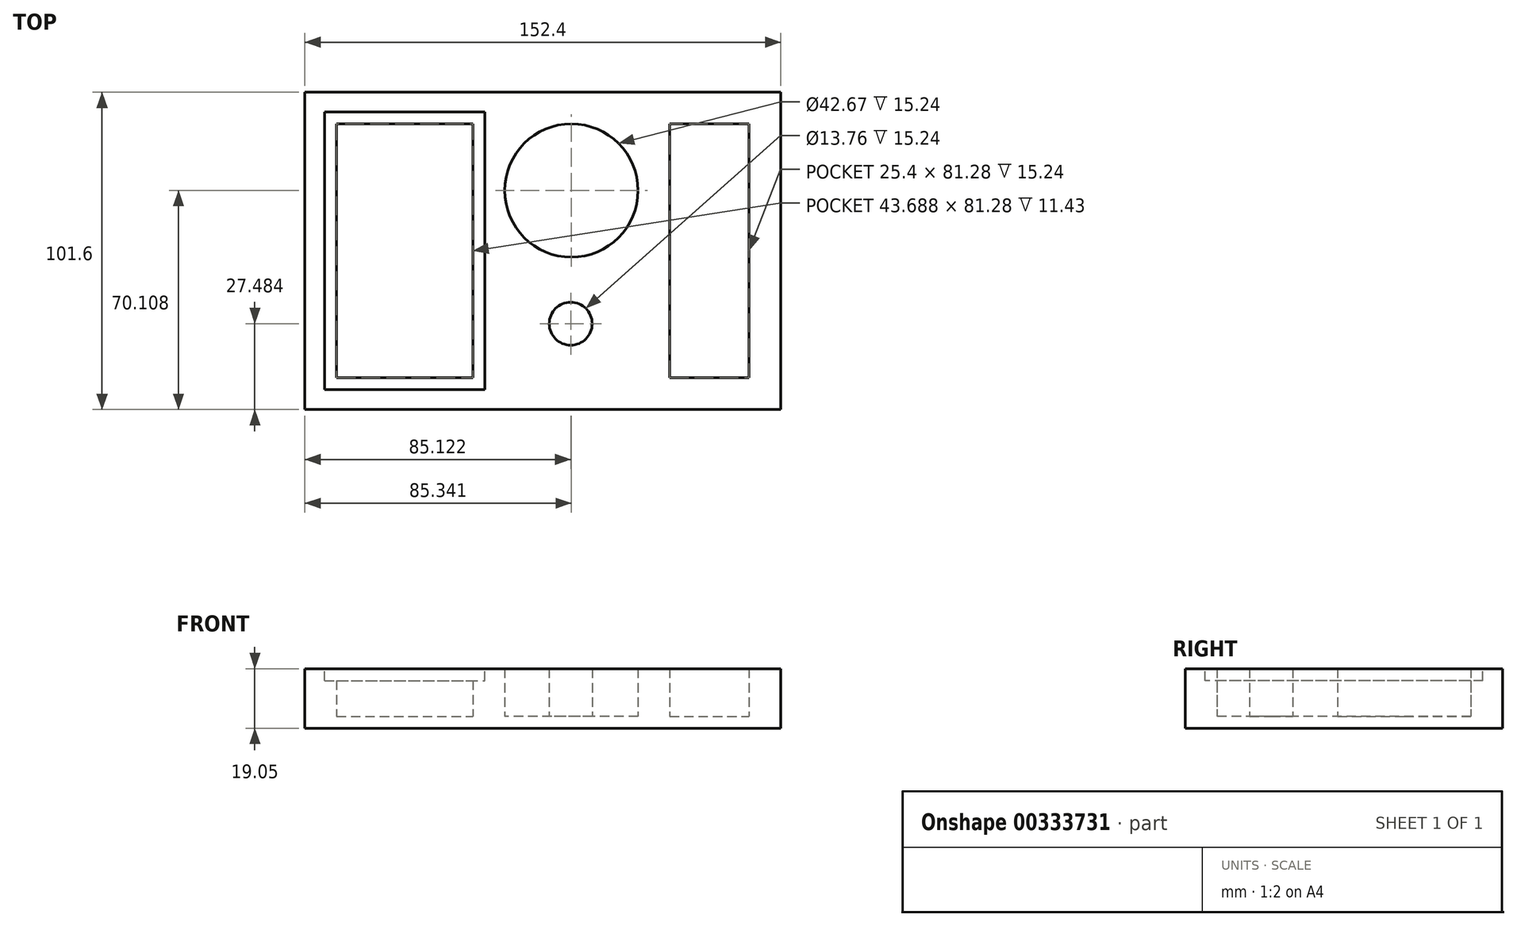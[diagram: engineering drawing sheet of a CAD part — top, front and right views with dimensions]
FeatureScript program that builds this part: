
annotation { "Feature Type Name" : "Feature", "Feature Type Description" : "" }
export const myFeature = defineFeature(function(context is Context, id is Id, definition is map)
    precondition{}
    {
        {
            var Q0;
            Q0=qCreatedBy(makeId("Top.planeOp"),FACE);
            var sketch = newSketch(context, id + "F0", { "sketchPlane" : qUnion([Q0])});
            skLineSegment(sketch, "E0.bottom", {"start": v(-90.13, 50.9) * mm, "end": v(62.27, 50.9) * mm});
            skLineSegment(sketch, "E0.top", {"start": v(-90.13, -50.7) * mm, "end": v(62.27, -50.7) * mm});
            skLineSegment(sketch, "E0.left", {"start": v(-90.13, 50.9) * mm, "end": v(-90.13, -50.7) * mm});
            skLineSegment(sketch, "E0.right", {"start": v(62.27, 50.9) * mm, "end": v(62.27, -50.7) * mm});
            skLineSegment(sketch, "E1.bottom", {"start": v(26.7, 40.74) * mm, "end": v(52.1, 40.74) * mm});
            skLineSegment(sketch, "E1.top", {"start": v(26.7, -40.54) * mm, "end": v(52.1, -40.54) * mm});
            skLineSegment(sketch, "E1.left", {"start": v(26.7, 40.74) * mm, "end": v(26.7, -40.54) * mm});
            skLineSegment(sketch, "E1.right", {"start": v(52.1, 40.74) * mm, "end": v(52.1, -40.54) * mm});
            skLineSegment(sketch, "E2.bottom", {"start": v(-79.97, 40.74) * mm, "end": v(16.55, 40.74) * mm});
            skLineSegment(sketch, "E2.top", {"start": v(-79.97, -40.54) * mm, "end": v(16.55, -40.54) * mm});
            skLineSegment(sketch, "E2.left", {"start": v(-79.97, 40.74) * mm, "end": v(-79.97, -40.54) * mm});
            skLineSegment(sketch, "E2.right", {"start": v(16.55, 40.74) * mm, "end": v(16.55, -40.54) * mm});
            skLineSegment(sketch, "E3.bottom", {"start": v(-79.97, 40.74) * mm, "end": v(-36.28, 40.74) * mm});
            skLineSegment(sketch, "E3.left", {"start": v(-79.97, 40.74) * mm, "end": v(-79.97, -4.47) * mm});
            skCircle(sketch, "E4", {"center": v(-4.79, 19.4) * mm, "radius": 21.34 * mm});
            skCircle(sketch, "E5", {"center": v(-5, -23.22) * mm, "radius": 6.88 * mm});
            skLineSegment(sketch, "E6", {"start": v(-36.28, 40.74) * mm, "end": v(-36.28, -40.54) * mm});
            skLineSegment(sketch, "E7", {"start": v(-26.12, 40.74) * mm, "end": v(-26.12, -40.54) * mm});
            skSolve(sketch);
        }
        {
            var Q0;
            Q0=makeQuery(id+"F0.imprint","IMPRINT",FACE,{"disambiguationData":[TD([[makeQuery(id+"F0.imprint","IMPRINT",EDGE,{"derivedFrom":sQuery(id+"F0.wireOp",EDGE,"E0.bottom")}),-1.0]])]});
            var Q1;
            Q1=makeQuery(id+"F0.imprint","IMPRINT",FACE,{"disambiguationData":[TD([[makeQuery(id+"F0.imprint","IMPRINT",EDGE,{"derivedFrom":sQuery(id+"F0.wireOp",EDGE,"E5")}),-1.0]])]});
            var Q2;
            {var subQ0=sQuery(id+"F0.wireOp",EDGE,"E2.right");var subQ1=sQuery(id+"F0.wireOp",EDGE,"E2.bottom");var subQ2=makeQuery(id+"F0.imprint","INTERSECT",VERTEX,{"derivedFrom":[subQ1,subQ0]});Q2=makeQuery(id+"F0.imprint","IMPRINT",FACE,{"disambiguationData":[TD([[makeQuery(id+"F0.imprint","IMPRINT",EDGE,{"disambiguationData":[TD([[subQ2,1.0]])],"derivedFrom":subQ1}),-1.0]])]});}
            var Q3;
            {var subQ0=sQuery(id+"F0.wireOp",EDGE,"E7");var subQ1=sQuery(id+"F0.wireOp",EDGE,"E2.bottom");var subQ2=makeQuery(id+"F0.imprint","INTERSECT",VERTEX,{"derivedFrom":[subQ1,subQ0]});Q3=makeQuery(id+"F0.imprint","IMPRINT",FACE,{"disambiguationData":[TD([[makeQuery(id+"F0.imprint","IMPRINT",EDGE,{"disambiguationData":[TD([[subQ2,-1.0]])],"derivedFrom":subQ1}),-1.0]])]});}
            var Q4;
            {var subQ4=sQuery(id+"F0.wireOp",EDGE,"E6");Q4=makeQuery(id+"F0.imprint","IMPRINT",FACE,{"disambiguationData":[TD([[makeQuery(id+"F0.imprint","IMPRINT",EDGE,{"derivedFrom":subQ4}),1.0]])]});}
            extrude(context, id + "F1", {"entities" : qUnion([Q0, Q1, Q2, Q3, Q4]), "depth" : 19.05 * mm});
        }
        {
            var Q0;
            {var subQ0=sQuery(id+"F0.wireOp",EDGE,"E2.left");Q0=makeQuery(id+"F0.imprint","IMPRINT",FACE,{"disambiguationData":[TD([[makeQuery(id+"F0.imprint","IMPRINT",EDGE,{"derivedFrom":subQ0}),1.0]])]});}
            var Q1;
            {var subQ0=sQuery(id+"F0.wireOp",EDGE,"E4");var subQ1=makeQuery(id+"F0.imprint","INTERSECT",VERTEX,{"derivedFrom":[sQuery(id+"F0.wireOp",EDGE,"E2.bottom"),subQ0]});Q1=makeQuery(id+"F0.imprint","IMPRINT",FACE,{"disambiguationData":[TD([[makeQuery(id+"F0.imprint","IMPRINT",EDGE,{"disambiguationData":[TD([[subQ1,1.0]])],"derivedFrom":subQ0}),1.0]])]});}
            var Q2;
            Q2=makeQuery(id+"F0.imprint","IMPRINT",FACE,{"disambiguationData":[TD([[makeQuery(id+"F0.imprint","IMPRINT",EDGE,{"derivedFrom":sQuery(id+"F0.wireOp",EDGE,"E5")}),1.0]])]});
            var Q3;
            Q3=makeQuery(id+"F0.imprint","IMPRINT",FACE,{"disambiguationData":[TD([[makeQuery(id+"F0.imprint","IMPRINT",EDGE,{"derivedFrom":sQuery(id+"F0.wireOp",EDGE,"E1.bottom")}),-1.0]])]});
            extrude(context, id + "F2", {"entities" : qUnion([Q0, Q1, Q2, Q3]), "operationType" : NewBodyOperationType.ADD, "depth" : 3.8 * mm});
        }
        {
            var Q0;
            Q0=makeQuery(id+"F1.opExtrude","CAP_FACE",FACE,{"disambiguationData":[OSD([sQuery(id+"F0.wireOp",EDGE,"E0.bottom"),sQuery(id+"F0.wireOp",EDGE,"E0.top"),sQuery(id+"F0.wireOp",EDGE,"E0.left"),sQuery(id+"F0.wireOp",EDGE,"E0.right"),sQuery(id+"F0.wireOp",EDGE,"E1.bottom"),sQuery(id+"F0.wireOp",EDGE,"E1.top"),sQuery(id+"F0.wireOp",EDGE,"E1.left"),sQuery(id+"F0.wireOp",EDGE,"E1.right"),sQuery(id+"F0.wireOp",EDGE,"E2.top"),sQuery(id+"F0.wireOp",EDGE,"E2.left"),sQuery(id+"F0.wireOp",EDGE,"E3.bottom"),sQuery(id+"F0.wireOp",EDGE,"E3.left"),sQuery(id+"F0.wireOp",EDGE,"E4"),sQuery(id+"F0.wireOp",EDGE,"E5"),sQuery(id+"F0.wireOp",EDGE,"E6")])],"isStart":false});
            var sketch = newSketch(context, id + "F3", { "sketchPlane" : qUnion([Q0])});
            skLineSegment(sketch, "E8.0", {"start": v(-32.47, 44.55) * mm, "end": v(-32.47, -44.35) * mm});
            skLineSegment(sketch, "E8.1", {"start": v(-83.78, 44.55) * mm, "end": v(-32.47, 44.55) * mm});
            skLineSegment(sketch, "E8.2", {"start": v(-83.78, 44.55) * mm, "end": v(-83.78, -44.35) * mm});
            skLineSegment(sketch, "E8.3", {"start": v(-83.78, -44.35) * mm, "end": v(-32.47, -44.35) * mm});
            skSolve(sketch);
        }
        {
            var Q0;
            Q0=makeQuery(id+"F3.imprint","IMPRINT",FACE,{"disambiguationData":[TD([[makeQuery(id+"F3.imprint","IMPRINT",EDGE,{"derivedFrom":makeQuery(id+"F1.opExtrude","CAP_EDGE",EDGE,{"disambiguationData":[OSD([sQuery(id+"F0.wireOp",EDGE,"E2.top")])],"isStart":false})}),1.0]])]});
            var Q1;
            Q1=makeQuery(id+"F3.imprint","IMPRINT",FACE,{"disambiguationData":[TD([[makeQuery(id+"F3.imprint","IMPRINT",EDGE,{"derivedFrom":sQuery(id+"F3.wireOp",EDGE,"E8.0")}),-1.0]])]});
            extrude(context, id + "F4", {"entities" : qUnion([Q0, Q1]), "operationType" : NewBodyOperationType.REMOVE, "oppositeDirection" : true, "depth" : 3.8 * mm});
        }
    });
